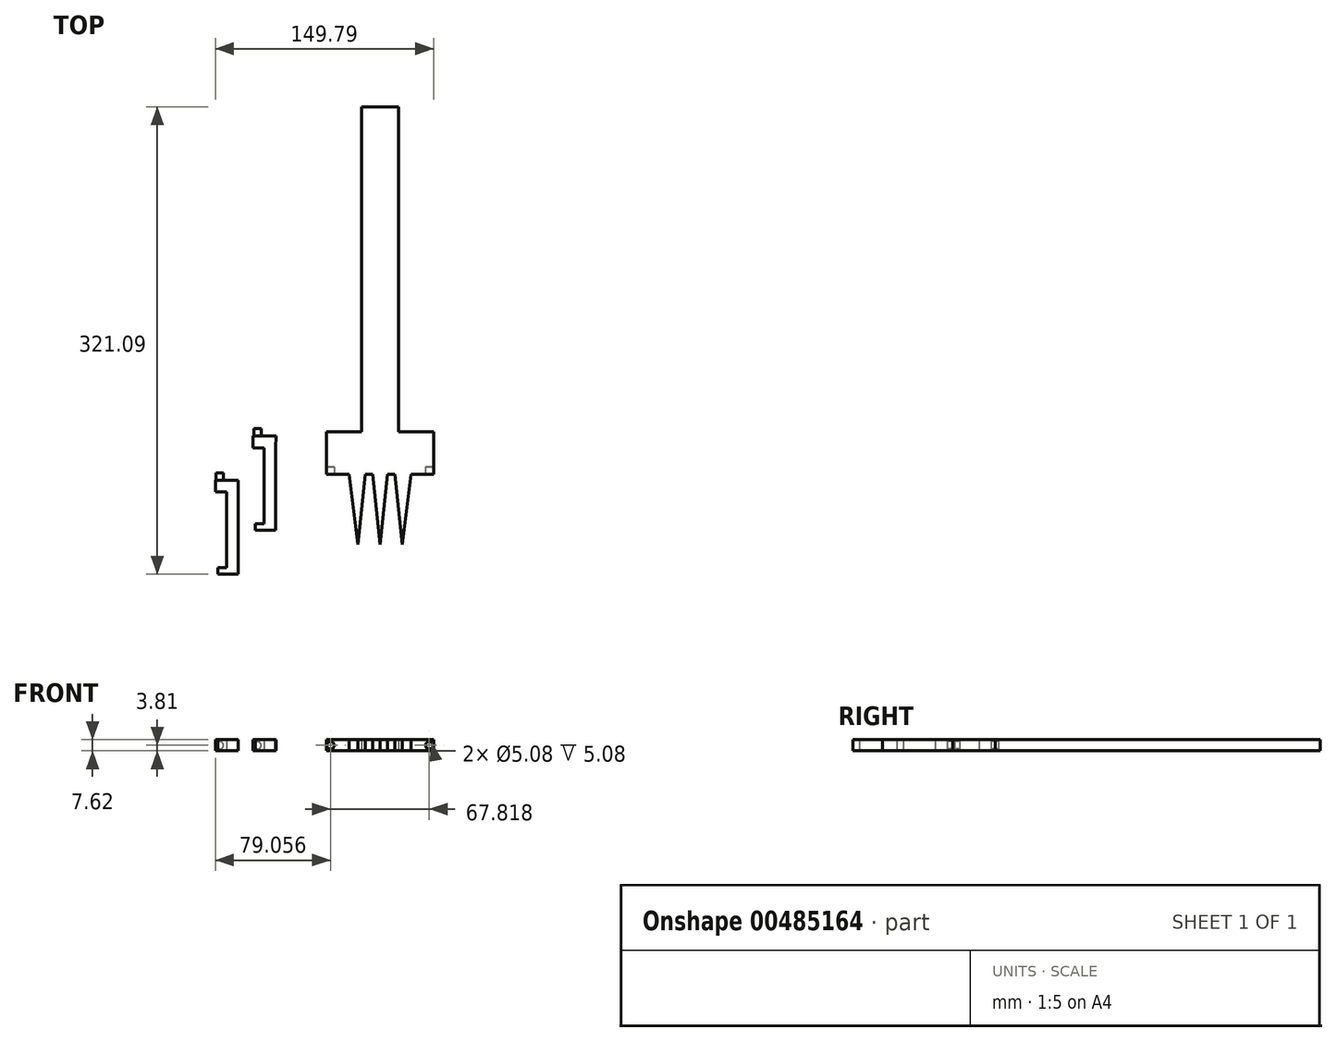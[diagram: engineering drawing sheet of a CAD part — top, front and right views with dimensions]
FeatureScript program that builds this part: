
annotation { "Feature Type Name" : "Feature", "Feature Type Description" : "" }
export const myFeature = defineFeature(function(context is Context, id is Id, definition is map)
    precondition{}
    {
        {
            var Q0;
            Q0=qCreatedBy(makeId("Top.planeOp"),FACE);
            var sketch = newSketch(context, id + "F0", { "sketchPlane" : qUnion([Q0])});
            skLineSegment(sketch, "E0", {"start": v(42, 63.5) * mm, "end": v(42, 0) * mm, "construction": true});
            skPoint(sketch, "E1", {"position": v(26.74, 8.89) * mm});
            skPoint(sketch, "E2", {"position": v(42, 8.89) * mm});
            skLineSegment(sketch, "E3", {"start": v(26.74, 8.89) * mm, "end": v(20.78, 57.15) * mm});
            skLineSegment(sketch, "E4", {"start": v(26.74, 8.89) * mm, "end": v(31.81, 57.15) * mm});
            skLineSegment(sketch, "E5", {"start": v(12.9, 57.15) * mm, "end": v(20.78, 57.15) * mm});
            skLineSegment(sketch, "E6", {"start": v(31.81, 57.15) * mm, "end": v(36.86, 57.15) * mm});
            skLineSegment(sketch, "E7", {"start": v(36.86, 57.15) * mm, "end": v(42, 8.89) * mm});
            skLineSegment(sketch, "E8.MirrorCS", {"start": v(47.13, 57.15) * mm, "end": v(42, 8.89) * mm});
            skPoint(sketch, "E9.MirrorP", {"position": v(57.24, 8.89) * mm});
            skLineSegment(sketch, "E10.MirrorCS", {"start": v(52.18, 57.15) * mm, "end": v(47.13, 57.15) * mm});
            skLineSegment(sketch, "E11.MirrorCS", {"start": v(71.1, 57.15) * mm, "end": v(63.2, 57.15) * mm});
            skLineSegment(sketch, "E12.MirrorCS", {"start": v(57.24, 8.89) * mm, "end": v(52.18, 57.15) * mm});
            skLineSegment(sketch, "E13.MirrorCS", {"start": v(57.24, 8.89) * mm, "end": v(63.2, 57.15) * mm});
            skLineSegment(sketch, "E14", {"start": v(12.9, 57.15) * mm, "end": v(12.9, 6.35) * mm});
            skLineSegment(sketch, "E15", {"start": v(12.9, 6.35) * mm, "end": v(18.85, 6.35) * mm});
            skLineSegment(sketch, "E16", {"start": v(18.85, 6.35) * mm, "end": v(18.85, 1.96) * mm});
            skLineSegment(sketch, "E17", {"start": v(18.85, 1.96) * mm, "end": v(5.16, 1.96) * mm});
            skLineSegment(sketch, "E18", {"start": v(5.16, 1.96) * mm, "end": v(5.16, 57.15) * mm});
            skLineSegment(sketch, "E19.MirrorCS", {"start": v(65.14, 6.35) * mm, "end": v(65.14, 1.96) * mm});
            skLineSegment(sketch, "E20.MirrorCS", {"start": v(71.1, 6.35) * mm, "end": v(65.14, 6.35) * mm});
            skLineSegment(sketch, "E21.MirrorCS", {"start": v(65.14, 1.96) * mm, "end": v(78.82, 1.96) * mm});
            skLineSegment(sketch, "E22.MirrorCS", {"start": v(71.1, 57.15) * mm, "end": v(71.1, 6.35) * mm});
            skLineSegment(sketch, "E23.MirrorCS", {"start": v(78.82, 1.96) * mm, "end": v(78.82, 57.15) * mm});
            skLineSegment(sketch, "E24", {"start": v(5.16, 57.15) * mm, "end": v(5.16, 63.5) * mm});
            skLineSegment(sketch, "E25", {"start": v(78.82, 57.15) * mm, "end": v(78.82, 63.5) * mm});
            skPoint(sketch, "E26.left.start.orphan", {"position": v(0, 0) * mm});
            skPoint(sketch, "E27.orphan", {"position": v(84.1, 63.5) * mm});
            skLineSegment(sketch, "E28.top", {"start": v(5.16, 86.36) * mm, "end": v(29.3, 86.36) * mm});
            skLineSegment(sketch, "E28.left", {"start": v(5.16, 63.5) * mm, "end": v(5.16, 86.36) * mm});
            skLineSegment(sketch, "E28.right", {"start": v(78.82, 63.5) * mm, "end": v(78.82, 86.36) * mm});
            skLineSegment(sketch, "E29.top", {"start": v(29.3, 309.63) * mm, "end": v(54.7, 309.63) * mm});
            skLineSegment(sketch, "E29.left", {"start": v(29.3, 86.36) * mm, "end": v(29.3, 309.63) * mm});
            skLineSegment(sketch, "E29.right", {"start": v(54.7, 86.36) * mm, "end": v(54.7, 309.63) * mm});
            skLineSegment(sketch, "E30.trimOffspring", {"start": v(54.7, 86.36) * mm, "end": v(78.82, 86.36) * mm});
            skSolve(sketch);
        }
        {
            var Q0;
            Q0=makeQuery(id+"F0.imprint","IMPRINT",FACE,{"disambiguationData":[TD([[makeQuery(id+"F0.imprint","IMPRINT",EDGE,{"derivedFrom":sQuery(id+"F0.wireOp",EDGE,"E3")}),-1.0]])]});
            extrude(context, id + "F1", {"entities" : qUnion([Q0]), "depth" : 101.6 * mm});
        }
        {
            var Q0;
            Q0=makeQuery(id+"F1.opExtrude","SWEPT_FACE",FACE,{"disambiguationData":[OSD([sQuery(id+"F0.wireOp",EDGE,"E29.right")])]});
            var sketch = newSketch(context, id + "F2", { "sketchPlane" : qUnion([Q0])});
            skLineSegment(sketch, "E31.0", {"start": v(86.36, 101.6) * mm, "end": v(86.36, 7.62) * mm});
            skLineSegment(sketch, "E31.1", {"start": v(86.36, 101.6) * mm, "end": v(309.63, 101.6) * mm});
            skLineSegment(sketch, "E31.2", {"start": v(86.36, 0) * mm, "end": v(309.63, 0) * mm});
            skLineSegment(sketch, "E31.3", {"start": v(309.63, 101.6) * mm, "end": v(309.63, 7.62) * mm});
            skLineSegment(sketch, "E32", {"start": v(86.36, 7.62) * mm, "end": v(309.63, 7.62) * mm});
            skPoint(sketch, "E33.orphan", {"position": v(86.36, 0) * mm});
            skLineSegment(sketch, "E34", {"start": v(86.36, 7.62) * mm, "end": v(1.96, 7.62) * mm});
            skLineSegment(sketch, "E35.0", {"start": v(1.96, 101.6) * mm, "end": v(1.96, 7.62) * mm});
            skLineSegment(sketch, "E35.1", {"start": v(1.96, 101.6) * mm, "end": v(86.36, 101.6) * mm});
            skPoint(sketch, "E36.orphan", {"position": v(0, 7.62) * mm});
            skPoint(sketch, "E37.orphan", {"position": v(1.96, 0) * mm});
            skSolve(sketch);
        }
        {
            var Q0;
            Q0 = qSketchRegion(id + "F2", true);
            extrude(context, id + "F3", {"entities" : qUnion([Q0]), "operationType" : NewBodyOperationType.REMOVE, "endBound" : BoundingType.THROUGH_ALL, "oppositeDirection" : true, "depth" : 25.4 * mm});
        }
        {
            var Q0;
            Q0=makeQuery(id+"F1.opExtrude","SWEPT_FACE",FACE,{"disambiguationData":[OSD([sQuery(id+"F0.wireOp",EDGE,"E23.MirrorCS"),sQuery(id+"F0.wireOp",EDGE,"E25"),sQuery(id+"F0.wireOp",EDGE,"E28.right")])]});
            var sketch = newSketch(context, id + "F4", { "sketchPlane" : qUnion([Q0])});
            skLineSegment(sketch, "E38.0", {"start": v(1.96, 101.6) * mm, "end": v(1.96, 7.62) * mm});
            skLineSegment(sketch, "E39.0", {"start": v(86.36, 101.6) * mm, "end": v(86.36, 7.62) * mm});
            skPoint(sketch, "E40.0", {"position": v(57.15, 101.6) * mm});
            skLineSegment(sketch, "E41.0", {"start": v(1.96, 101.6) * mm, "end": v(86.36, 101.6) * mm});
            skLineSegment(sketch, "E42", {"start": v(1.96, 7.62) * mm, "end": v(86.36, 7.62) * mm});
            skPoint(sketch, "E43.0.end.orphan", {"position": v(86.36, 0) * mm});
            skPoint(sketch, "E43.0.start.orphan", {"position": v(1.96, 0) * mm});
            skSolve(sketch);
        }
        {
            var Q0;
            Q0=makeQuery(id+"F4.imprint","IMPRINT",FACE,{"disambiguationData":[TD([[makeQuery(id+"F4.imprint","IMPRINT",EDGE,{"derivedFrom":sQuery(id+"F4.wireOp",EDGE,"E38.0")}),1.0]])]});
            extrude(context, id + "F5", {"entities" : qUnion([Q0]), "operationType" : NewBodyOperationType.REMOVE, "endBound" : BoundingType.THROUGH_ALL, "oppositeDirection" : true, "depth" : 25.4 * mm});
        }
        {
            var Q0;
            Q0=makeQuery(id+"F5.boolean.opBoolean","MERGE",FACE,{"derivedFrom":[makeQuery(id+"F3.boolean.opBoolean","COPY",FACE,{"derivedFrom":makeQuery(id+"F3.opExtrude","SWEPT_FACE",FACE,{"disambiguationData":[OSD([sQuery(id+"F2.wireOp",EDGE,"E32"),sQuery(id+"F2.wireOp",EDGE,"E34")])]})}),makeQuery(id+"F5.opExtrude","SWEPT_FACE",FACE,{"disambiguationData":[OSD([sQuery(id+"F4.wireOp",EDGE,"E42")])]})]});
            var sketch = newSketch(context, id + "F6", { "sketchPlane" : qUnion([Q0])});
            skLineSegment(sketch, "E44.0", {"start": v(5.16, 1.96) * mm, "end": v(5.16, 57.15) * mm});
            skLineSegment(sketch, "E45.0", {"start": v(12.9, 57.15) * mm, "end": v(12.9, 6.35) * mm});
            skLineSegment(sketch, "E46.0", {"start": v(5.16, 1.96) * mm, "end": v(18.85, 1.96) * mm});
            skPoint(sketch, "E47.0", {"position": v(18.85, 6.35) * mm});
            skLineSegment(sketch, "E48.0", {"start": v(18.85, 6.35) * mm, "end": v(18.85, 1.96) * mm});
            skLineSegment(sketch, "E49.0", {"start": v(71.1, 6.35) * mm, "end": v(71.1, 57.15) * mm});
            skLineSegment(sketch, "E50.0", {"start": v(65.14, 6.35) * mm, "end": v(71.1, 6.35) * mm});
            skLineSegment(sketch, "E51.0", {"start": v(65.14, 1.96) * mm, "end": v(65.14, 6.35) * mm});
            skLineSegment(sketch, "E52.0", {"start": v(65.14, 1.96) * mm, "end": v(78.82, 1.96) * mm});
            skLineSegment(sketch, "E53.0", {"start": v(78.82, 1.96) * mm, "end": v(78.82, 57.15) * mm});
            skLineSegment(sketch, "E54", {"start": v(12.9, 57.15) * mm, "end": v(5.16, 57.15) * mm});
            skLineSegment(sketch, "E55", {"start": v(71.1, 57.15) * mm, "end": v(78.82, 57.15) * mm});
            skPoint(sketch, "E56.orphan", {"position": v(5.16, 86.36) * mm});
            skPoint(sketch, "E57.orphan", {"position": v(78.82, 86.36) * mm});
            skSolve(sketch);
        }
        {
            var Q0;
            Q0=makeQuery(id+"F6.imprint","IMPRINT",FACE,{"disambiguationData":[TD([[makeQuery(id+"F6.imprint","IMPRINT",EDGE,{"derivedFrom":sQuery(id+"F6.wireOp",EDGE,"E44.0")}),-1.0]])]});
            var Q1;
            Q1=makeQuery(id+"F6.imprint","IMPRINT",FACE,{"disambiguationData":[TD([[makeQuery(id+"F6.imprint","IMPRINT",EDGE,{"derivedFrom":sQuery(id+"F6.wireOp",EDGE,"E49.0")}),-1.0]])]});
            extrude(context, id + "F7", {"entities" : qUnion([Q0, Q1]), "operationType" : NewBodyOperationType.REMOVE, "endBound" : BoundingType.THROUGH_ALL, "oppositeDirection" : true, "depth" : 25.4 * mm});
        }
        {
            var Q0;
            Q0=qCreatedBy(makeId("Top.planeOp"),FACE);
            var sketch = newSketch(context, id + "F8", { "sketchPlane" : qUnion([Q0])});
            skLineSegment(sketch, "E58.MirrorCS", {"start": v(-69.45, -6.97) * mm, "end": v(-69.45, -11.46) * mm});
            skLineSegment(sketch, "E59.MirrorCS", {"start": v(-63.35, -6.97) * mm, "end": v(-69.45, -6.97) * mm});
            skLineSegment(sketch, "E60.MirrorCS", {"start": v(-69.45, -11.46) * mm, "end": v(-55.43, -11.46) * mm});
            skLineSegment(sketch, "E61.MirrorCS", {"start": v(-63.35, 45.07) * mm, "end": v(-63.35, -6.97) * mm});
            skLineSegment(sketch, "E62.MirrorCS", {"start": v(-55.43, -11.46) * mm, "end": v(-55.43, 45.07) * mm});
            skLineSegment(sketch, "E63", {"start": v(-63.35, 45.07) * mm, "end": v(-70.97, 45.07) * mm});
            skLineSegment(sketch, "E64", {"start": v(-70.97, 45.07) * mm, "end": v(-70.97, 53.27) * mm});
            skLineSegment(sketch, "E65", {"start": v(-70.97, 53.27) * mm, "end": v(-55.36, 53.27) * mm});
            skLineSegment(sketch, "E66", {"start": v(-55.36, 53.27) * mm, "end": v(-55.43, 45.07) * mm});
            skLineSegment(sketch, "E67.MirrorCS", {"start": v(-43.54, 23.26) * mm, "end": v(-43.54, 18.76) * mm});
            skLineSegment(sketch, "E68.MirrorCS", {"start": v(-37.44, 23.26) * mm, "end": v(-43.54, 23.26) * mm});
            skLineSegment(sketch, "E69.MirrorCS", {"start": v(-43.54, 18.76) * mm, "end": v(-29.52, 18.76) * mm});
            skLineSegment(sketch, "E70.MirrorCS", {"start": v(-37.44, 75.3) * mm, "end": v(-37.44, 23.26) * mm});
            skLineSegment(sketch, "E71.MirrorCS", {"start": v(-29.52, 18.76) * mm, "end": v(-29.52, 75.3) * mm});
            skLineSegment(sketch, "E72", {"start": v(-37.44, 75.3) * mm, "end": v(-45.06, 75.3) * mm});
            skLineSegment(sketch, "E73", {"start": v(-45.06, 75.3) * mm, "end": v(-45.06, 83.5) * mm});
            skLineSegment(sketch, "E74", {"start": v(-45.06, 83.5) * mm, "end": v(-29.44, 83.5) * mm});
            skLineSegment(sketch, "E75", {"start": v(-29.44, 83.5) * mm, "end": v(-29.52, 75.3) * mm});
            skSolve(sketch);
        }
        {
            var Q0;
            Q0=makeQuery(id+"F8.imprint","IMPRINT",FACE,{"disambiguationData":[TD([[makeQuery(id+"F8.imprint","IMPRINT",EDGE,{"derivedFrom":sQuery(id+"F8.wireOp",EDGE,"E58.MirrorCS")}),1.0]])]});
            var Q1;
            Q1=makeQuery(id+"F8.imprint","IMPRINT",FACE,{"disambiguationData":[TD([[makeQuery(id+"F8.imprint","IMPRINT",EDGE,{"derivedFrom":sQuery(id+"F8.wireOp",EDGE,"E67.MirrorCS")}),1.0]])]});
            extrude(context, id + "F9", {"entities" : qUnion([Q0, Q1]), "depth" : 7.62 * mm});
        }
        {
            var Q0;
            Q0=makeQuery(id+"F9.opExtrude","SWEPT_FACE",FACE,{"disambiguationData":[OSD([sQuery(id+"F8.wireOp",EDGE,"E65")])]});
            var sketch = newSketch(context, id + "F10", { "sketchPlane" : qUnion([Q0])});
            skCircle(sketch, "E76", {"center": v(68.05, 3.81) * mm, "radius": 2.54 * mm});
            skSolve(sketch);
        }
        {
            var Q0;
            Q0=makeQuery(id+"F10.imprint","IMPRINT",FACE,{"disambiguationData":[TD([[makeQuery(id+"F10.imprint","IMPRINT",EDGE,{"derivedFrom":sQuery(id+"F10.wireOp",EDGE,"E76")}),1.0]])]});
            extrude(context, id + "F11", {"entities" : qUnion([Q0]), "operationType" : NewBodyOperationType.ADD, "depth" : 5.08 * mm});
        }
        {
            var Q0;
            Q0=makeQuery(id+"F9.opExtrude","SWEPT_FACE",FACE,{"disambiguationData":[OSD([sQuery(id+"F8.wireOp",EDGE,"E74")])]});
            var sketch = newSketch(context, id + "F12", { "sketchPlane" : qUnion([Q0])});
            skCircle(sketch, "E77", {"center": v(42.14, 3.8) * mm, "radius": 2.54 * mm});
            skSolve(sketch);
        }
        {
            var Q0;
            Q0=makeQuery(id+"F12.imprint","IMPRINT",FACE,{"disambiguationData":[TD([[makeQuery(id+"F12.imprint","IMPRINT",EDGE,{"derivedFrom":sQuery(id+"F12.wireOp",EDGE,"E77")}),1.0]])]});
            extrude(context, id + "F13", {"entities" : qUnion([Q0]), "operationType" : NewBodyOperationType.ADD, "depth" : 5.08 * mm});
        }
        {
            var Q0;
            Q0=makeQuery(id+"F7.boolean.opBoolean","MERGE",FACE,{"derivedFrom":[makeQuery(id+"F1.opExtrude","SWEPT_FACE",FACE,{"disambiguationData":[OSD([sQuery(id+"F0.wireOp",EDGE,"E5")])]}),makeQuery(id+"F7.opExtrude","SWEPT_FACE",FACE,{"disambiguationData":[OSD([sQuery(id+"F6.wireOp",EDGE,"E54")])]})]});
            var sketch = newSketch(context, id + "F14", { "sketchPlane" : qUnion([Q0])});
            skCircle(sketch, "E78", {"center": v(8.09, 3.81) * mm, "radius": 2.54 * mm});
            skCircle(sketch, "E79.MirrorC", {"center": v(75.9, 3.81) * mm, "radius": 2.54 * mm});
            skSolve(sketch);
        }
        {
            var Q0;
            Q0 = qSketchRegion(id + "F14", true);
            extrude(context, id + "F15", {"entities" : qUnion([Q0]), "operationType" : NewBodyOperationType.REMOVE, "oppositeDirection" : true, "depth" : 5.08 * mm});
        }
    });
